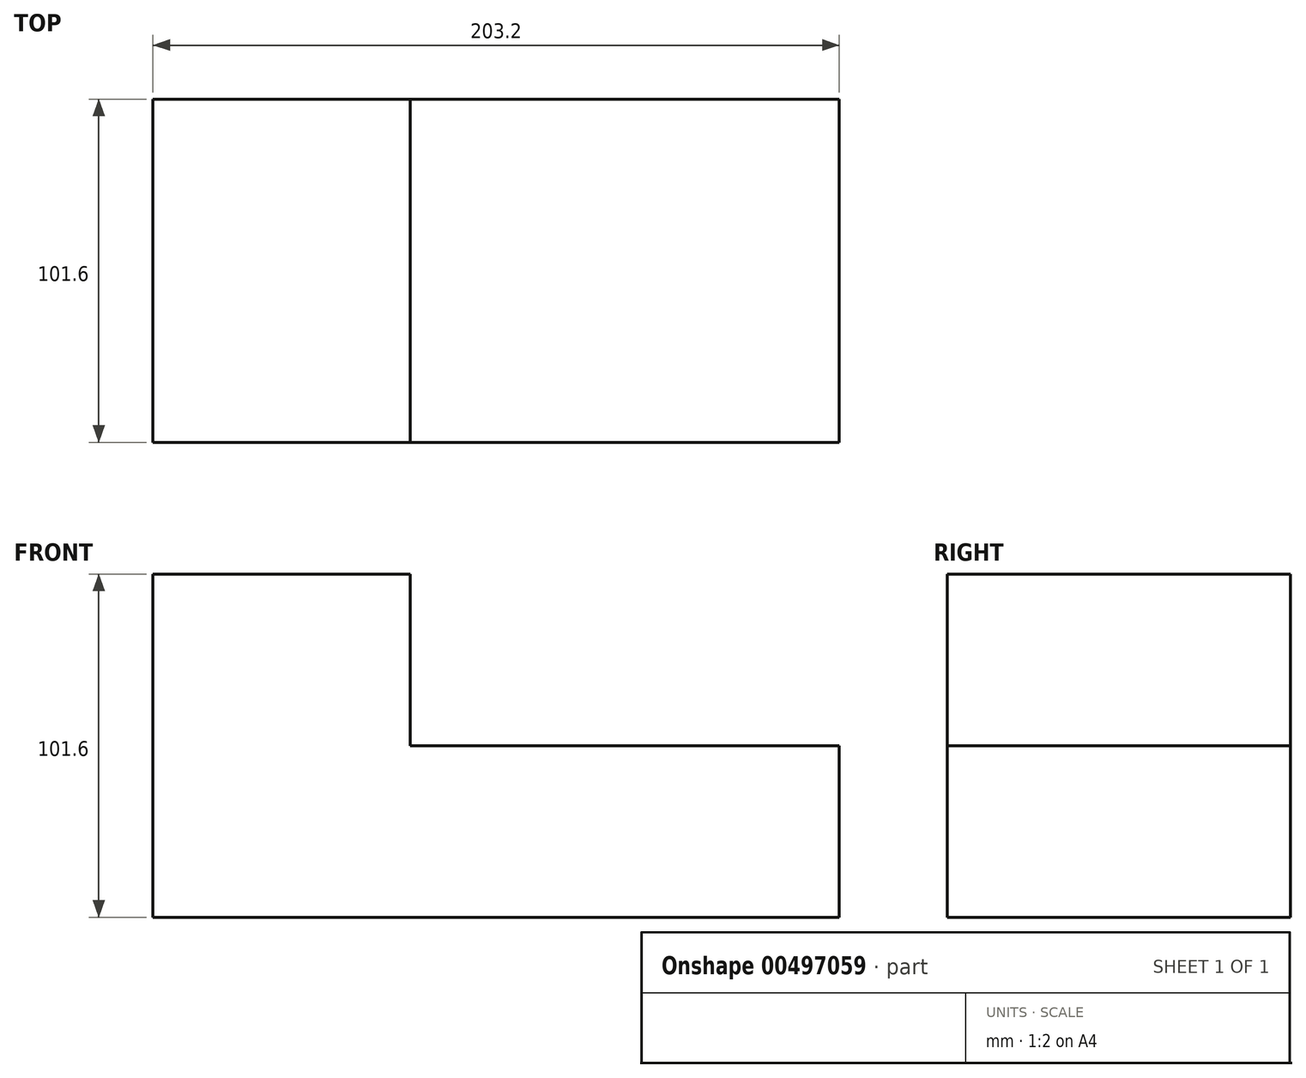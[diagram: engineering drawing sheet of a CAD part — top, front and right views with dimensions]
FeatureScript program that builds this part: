
annotation { "Feature Type Name" : "Feature", "Feature Type Description" : "" }
export const myFeature = defineFeature(function(context is Context, id is Id, definition is map)
    precondition{}
    {
        {
            var Q0;
            Q0=qCreatedBy(makeId("Front.planeOp"),FACE);
            var sketch = newSketch(context, id + "F0", { "sketchPlane" : qUnion([Q0])});
            skLineSegment(sketch, "E0.bottom", {"start": v(-85.12, 1.68) * mm, "end": v(118.08, 1.68) * mm});
            skLineSegment(sketch, "E0.top", {"start": v(-85.12, -49.12) * mm, "end": v(118.08, -49.12) * mm});
            skLineSegment(sketch, "E0.left", {"start": v(-85.12, 1.68) * mm, "end": v(-85.12, -49.12) * mm});
            skLineSegment(sketch, "E0.right", {"start": v(118.08, 1.68) * mm, "end": v(118.08, -49.12) * mm});
            skLineSegment(sketch, "E1.bottom", {"start": v(-85.12, 1.68) * mm, "end": v(-8.92, 1.68) * mm});
            skLineSegment(sketch, "E1.top", {"start": v(-85.12, 52.48) * mm, "end": v(-8.92, 52.48) * mm});
            skLineSegment(sketch, "E1.left", {"start": v(-85.12, 1.68) * mm, "end": v(-85.12, 52.48) * mm});
            skLineSegment(sketch, "E1.right", {"start": v(-8.92, 1.68) * mm, "end": v(-8.92, 52.48) * mm});
            skSolve(sketch);
        }
        {
            var Q0;
            Q0 = qSketchRegion(id + "F0", true);
            extrude(context, id + "F1", {"entities" : qUnion([Q0]), "depth" : 101.6 * mm});
        }
    });
